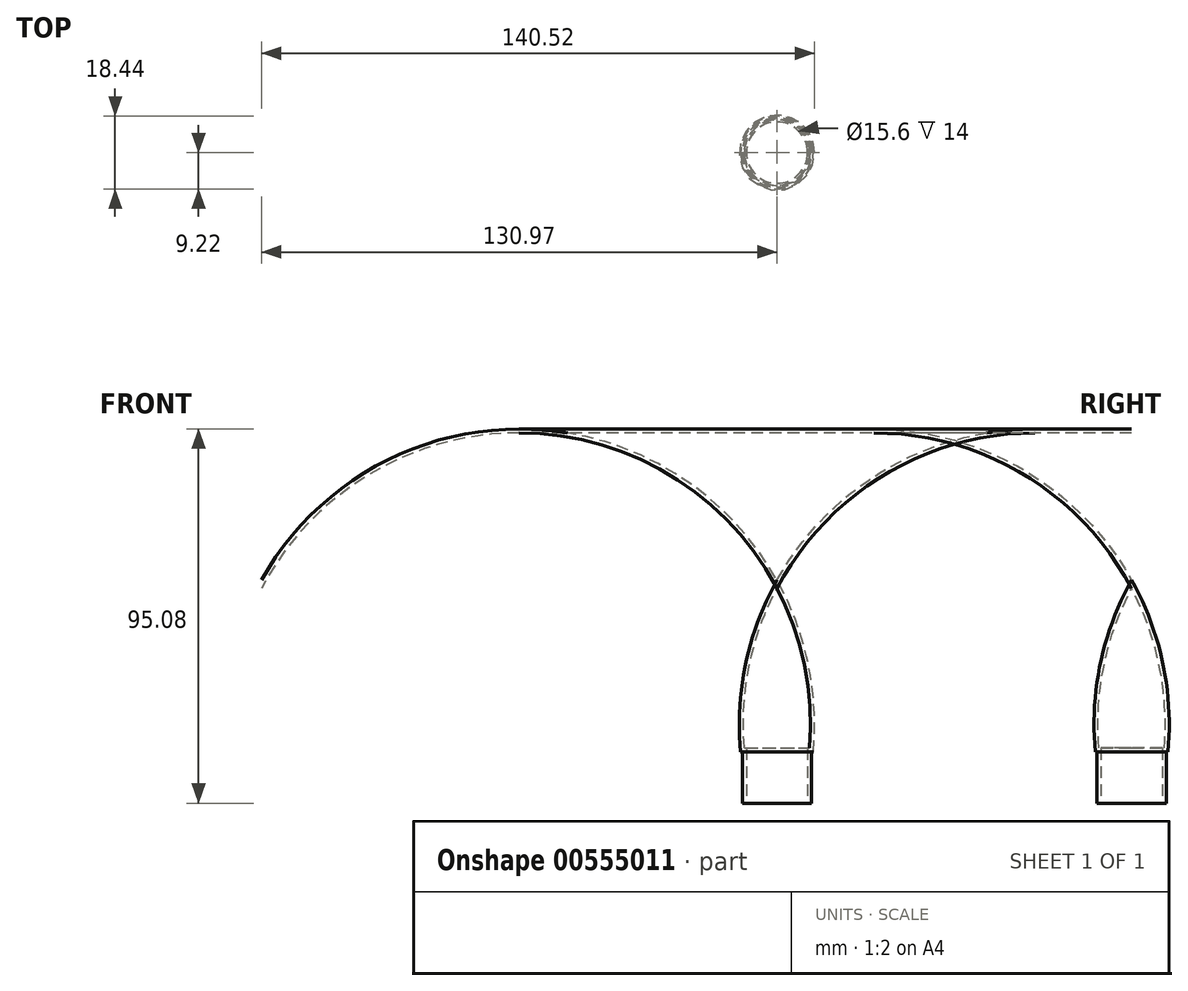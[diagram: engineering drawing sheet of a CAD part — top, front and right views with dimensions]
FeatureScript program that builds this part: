
annotation { "Feature Type Name" : "Feature", "Feature Type Description" : "" }
export const myFeature = defineFeature(function(context is Context, id is Id, definition is map)
    precondition{}
    {
        {
            var Q0;
            Q0=qCreatedBy(makeId("Front.planeOp"),FACE);
            var sketch = newSketch(context, id + "F0", { "sketchPlane" : qUnion([Q0])});
            skLineSegment(sketch, "E0", {"start": v(0, 25.35) * mm, "end": v(0, 79.85) * mm});
            skLineSegment(sketch, "E1", {"start": v(7.8, 25.27) * mm, "end": v(7.8, 39.27) * mm});
            skLineSegment(sketch, "E2", {"start": v(7.8, 39.27) * mm, "end": v(8.3, 39.27) * mm});
            skArc(sketch, "E3", {"start": v(8.3, 39.27) * mm, "mid": v(7.05, 60.15) * mm, "end": v(0, 79.85) * mm});
            skArc(sketch, "E4.0", {"start": v(9.22, 38.27) * mm, "mid": v(7.93, 60.8) * mm, "end": v(0, 81.94) * mm});
            skLineSegment(sketch, "E4.1", {"start": v(8.8, 38.27) * mm, "end": v(9.22, 38.27) * mm});
            skLineSegment(sketch, "E4.2", {"start": v(8.8, 25.27) * mm, "end": v(8.8, 38.27) * mm});
            skLineSegment(sketch, "E5", {"start": v(0, 79.85) * mm, "end": v(0, 81.94) * mm});
            skLineSegment(sketch, "E6", {"start": v(8.8, 25.27) * mm, "end": v(7.8, 25.27) * mm});
            skPoint(sketch, "E7.orphan", {"position": v(0, 0) * mm});
            skSolve(sketch);
        }
        {
            var Q0;
            Q0=makeQuery(id+"F0.imprint","IMPRINT",FACE,{"disambiguationData":[TD([[makeQuery(id+"F0.imprint","IMPRINT",EDGE,{"derivedFrom":sQuery(id+"F0.wireOp",EDGE,"E1")}),-1.0]])]});
            var Q1;
            Q1=sQuery(id+"F0.wireOp",EDGE,"E0");
            revolve(context, id + "F1", {"entities" : qUnion([Q0]), "axis" : qUnion([Q1]), "revolveType" : RevolveType.FULL});
        }
    });
